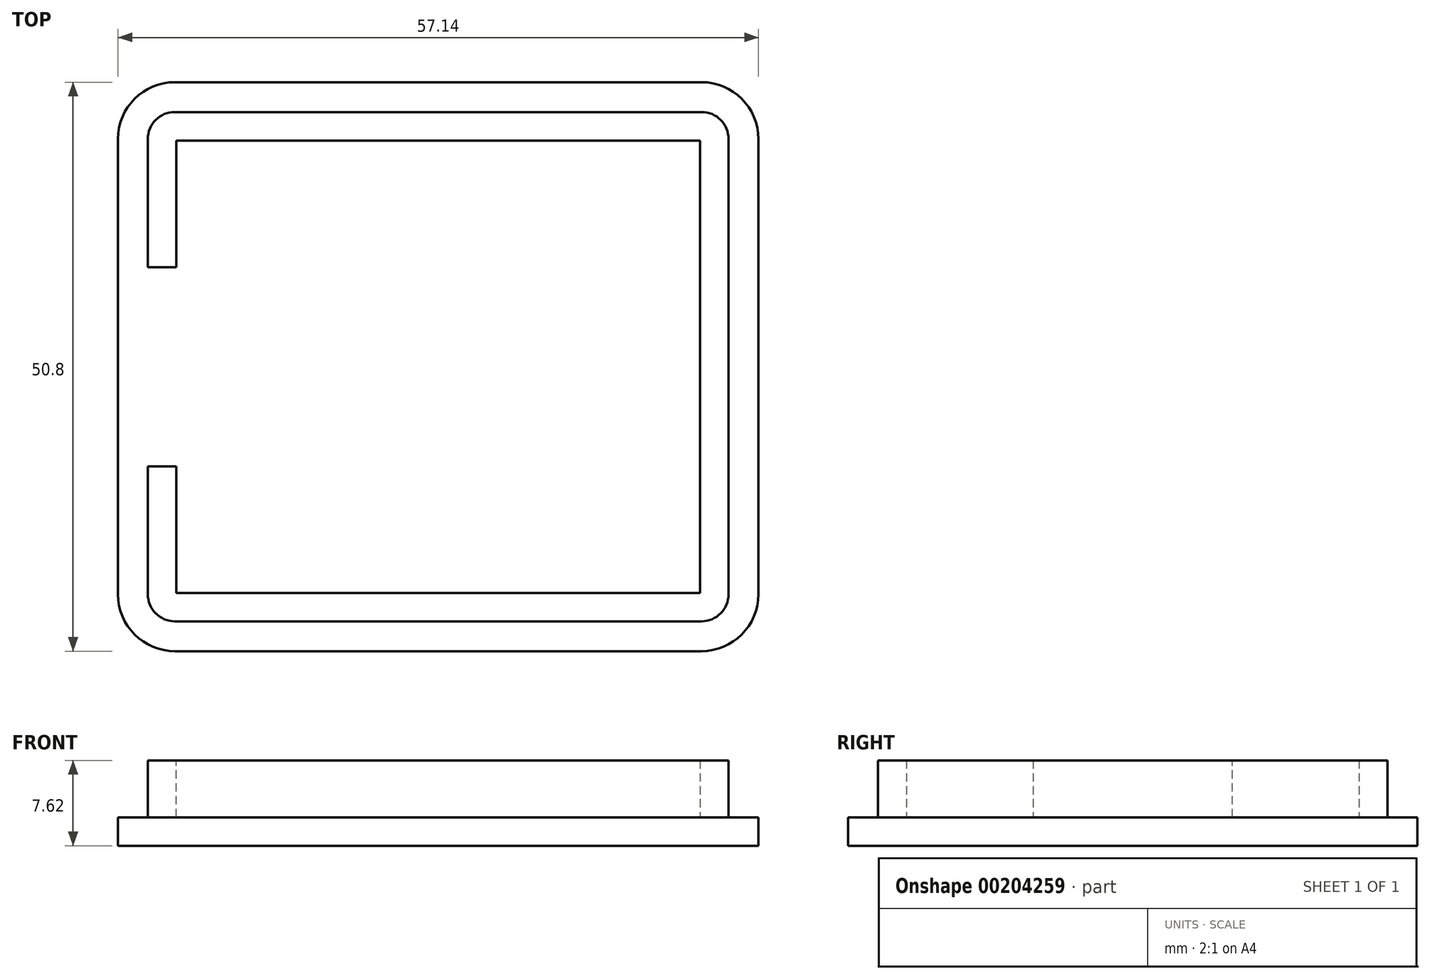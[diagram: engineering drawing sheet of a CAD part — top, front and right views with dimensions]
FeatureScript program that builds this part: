
annotation { "Feature Type Name" : "Feature", "Feature Type Description" : "" }
export const myFeature = defineFeature(function(context is Context, id is Id, definition is map)
    precondition{}
    {
        {
            var Q0;
            Q0=qCreatedBy(makeId("Top.planeOp"),FACE);
            var sketch = newSketch(context, id + "F0", { "sketchPlane" : qUnion([Q0])});
            skLineSegment(sketch, "E0.bottom", {"start": v(28.58, -25.4) * mm, "end": v(-28.58, -25.4) * mm});
            skLineSegment(sketch, "E0.top", {"start": v(28.58, 25.4) * mm, "end": v(-28.58, 25.4) * mm});
            skLineSegment(sketch, "E0.left", {"start": v(28.58, -25.4) * mm, "end": v(28.58, 25.4) * mm});
            skLineSegment(sketch, "E0.right", {"start": v(-28.58, -25.4) * mm, "end": v(-28.58, 25.4) * mm});
            skPoint(sketch, "E0.middle", {"position": v(0, 0) * mm});
            skSolve(sketch);
        }
        {
            var Q0;
            Q0=makeQuery(id+"F0.imprint","IMPRINT",FACE,{"disambiguationData":[TD([[makeQuery(id+"F0.imprint","IMPRINT",EDGE,{"derivedFrom":sQuery(id+"F0.wireOp",EDGE,"E0.bottom")}),-1.0]])]});
            extrude(context, id + "F1", {"entities" : qUnion([Q0]), "depth" : 2.54 * mm});
        }
        {
            var Q0;
            Q0=makeQuery(id+"F1.opExtrude","SWEPT_EDGE",EDGE,{"disambiguationData":[OSD([sQuery(id+"F0.wireOp",EDGE,"E0.top"),sQuery(id+"F0.wireOp",EDGE,"E0.right")])]});
            var Q1;
            Q1=makeQuery(id+"F1.opExtrude","SWEPT_EDGE",EDGE,{"disambiguationData":[OSD([sQuery(id+"F0.wireOp",EDGE,"E0.top"),sQuery(id+"F0.wireOp",EDGE,"E0.left")])]});
            var Q2;
            Q2=makeQuery(id+"F1.opExtrude","SWEPT_EDGE",EDGE,{"disambiguationData":[OSD([sQuery(id+"F0.wireOp",EDGE,"E0.bottom"),sQuery(id+"F0.wireOp",EDGE,"E0.left")])]});
            var Q3;
            Q3=makeQuery(id+"F1.opExtrude","SWEPT_EDGE",EDGE,{"disambiguationData":[OSD([sQuery(id+"F0.wireOp",EDGE,"E0.bottom"),sQuery(id+"F0.wireOp",EDGE,"E0.right")])]});
            fillet(context, id + "F2", {"entities" : qUnion([Q0, Q1, Q2, Q3]), "radius" : 5.08 * mm, "tangentPropagation" : true, "allowEdgeOverflow" : false});
        }
        {
            var Q0;
            Q0=makeQuery(id+"F1.opExtrude","CAP_FACE",FACE,{"disambiguationData":[OSD([sQuery(id+"F0.wireOp",EDGE,"E0.bottom"),sQuery(id+"F0.wireOp",EDGE,"E0.top"),sQuery(id+"F0.wireOp",EDGE,"E0.left"),sQuery(id+"F0.wireOp",EDGE,"E0.right")])],"isStart":false});
            var sketch = newSketch(context, id + "F3", { "sketchPlane" : qUnion([Q0])});
            skArc(sketch, "E1.0", {"start": v(25.9, 20.32) * mm, "mid": v(25.2, 22.03) * mm, "end": v(23.5, 22.73) * mm});
            skLineSegment(sketch, "E1.1", {"start": v(25.9, -20.32) * mm, "end": v(25.9, 20.32) * mm});
            skLineSegment(sketch, "E1.2", {"start": v(23.5, 22.73) * mm, "end": v(-23.5, 22.73) * mm});
            skArc(sketch, "E1.3", {"start": v(23.5, -22.73) * mm, "mid": v(25.2, -22.03) * mm, "end": v(25.9, -20.32) * mm});
            skArc(sketch, "E1.4", {"start": v(-23.5, 22.73) * mm, "mid": v(-25.2, 22.03) * mm, "end": v(-25.9, 20.32) * mm});
            skLineSegment(sketch, "E1.5", {"start": v(-25.9, -20.32) * mm, "end": v(-25.9, 20.32) * mm});
            skArc(sketch, "E1.6", {"start": v(-25.9, -20.32) * mm, "mid": v(-25.2, -22.03) * mm, "end": v(-23.5, -22.73) * mm});
            skLineSegment(sketch, "E1.7", {"start": v(23.5, -22.73) * mm, "end": v(-23.5, -22.73) * mm});
            skLineSegment(sketch, "E2.bottom", {"start": v(23.37, -20.2) * mm, "end": v(-23.37, -20.2) * mm});
            skLineSegment(sketch, "E2.top", {"start": v(23.37, 20.2) * mm, "end": v(-23.37, 20.2) * mm});
            skLineSegment(sketch, "E2.left", {"start": v(23.37, -20.2) * mm, "end": v(23.37, 20.2) * mm});
            skLineSegment(sketch, "E2.right", {"start": v(-23.37, -20.2) * mm, "end": v(-23.37, 20.2) * mm});
            skPoint(sketch, "E2.middle", {"position": v(0, 0) * mm});
            skSolve(sketch);
        }
        {
            var Q0;
            Q0=makeQuery(id+"F3.imprint","IMPRINT",FACE,{"disambiguationData":[TD([[makeQuery(id+"F3.imprint","IMPRINT",EDGE,{"derivedFrom":sQuery(id+"F3.wireOp",EDGE,"E1.0")}),1.0]])]});
            extrude(context, id + "F4", {"entities" : qUnion([Q0]), "operationType" : NewBodyOperationType.ADD, "depth" : 5.08 * mm});
        }
        {
            var Q0;
            Q0=makeQuery(id+"F4.opExtrude","SWEPT_FACE",FACE,{"disambiguationData":[OSD([sQuery(id+"F3.wireOp",EDGE,"E1.5")])]});
            var sketch = newSketch(context, id + "F5", { "sketchPlane" : qUnion([Q0])});
            skLineSegment(sketch, "E3.bottom", {"start": v(-8.89, 7.62) * mm, "end": v(8.9, 7.62) * mm});
            skLineSegment(sketch, "E3.top", {"start": v(-8.89, 2.54) * mm, "end": v(8.9, 2.54) * mm});
            skLineSegment(sketch, "E3.left", {"start": v(-8.89, 7.62) * mm, "end": v(-8.89, 2.54) * mm});
            skLineSegment(sketch, "E3.right", {"start": v(8.9, 7.62) * mm, "end": v(8.9, 2.54) * mm});
            skSolve(sketch);
        }
        {
            var Q0;
            Q0 = qSketchRegion(id + "F5", true);
            var Q1;
            Q1=makeQuery(id+"F4.opExtrude","SWEPT_FACE",FACE,{"disambiguationData":[OSD([sQuery(id+"F3.wireOp",EDGE,"E2.right")])]});
            extrude(context, id + "F6", {"entities" : qUnion([Q0]), "operationType" : NewBodyOperationType.REMOVE, "endBound" : BoundingType.UP_TO_SURFACE, "oppositeDirection" : true, "endBoundEntityFace" : qUnion([Q1]), "depth" : 25.4 * mm});
        }
    });
